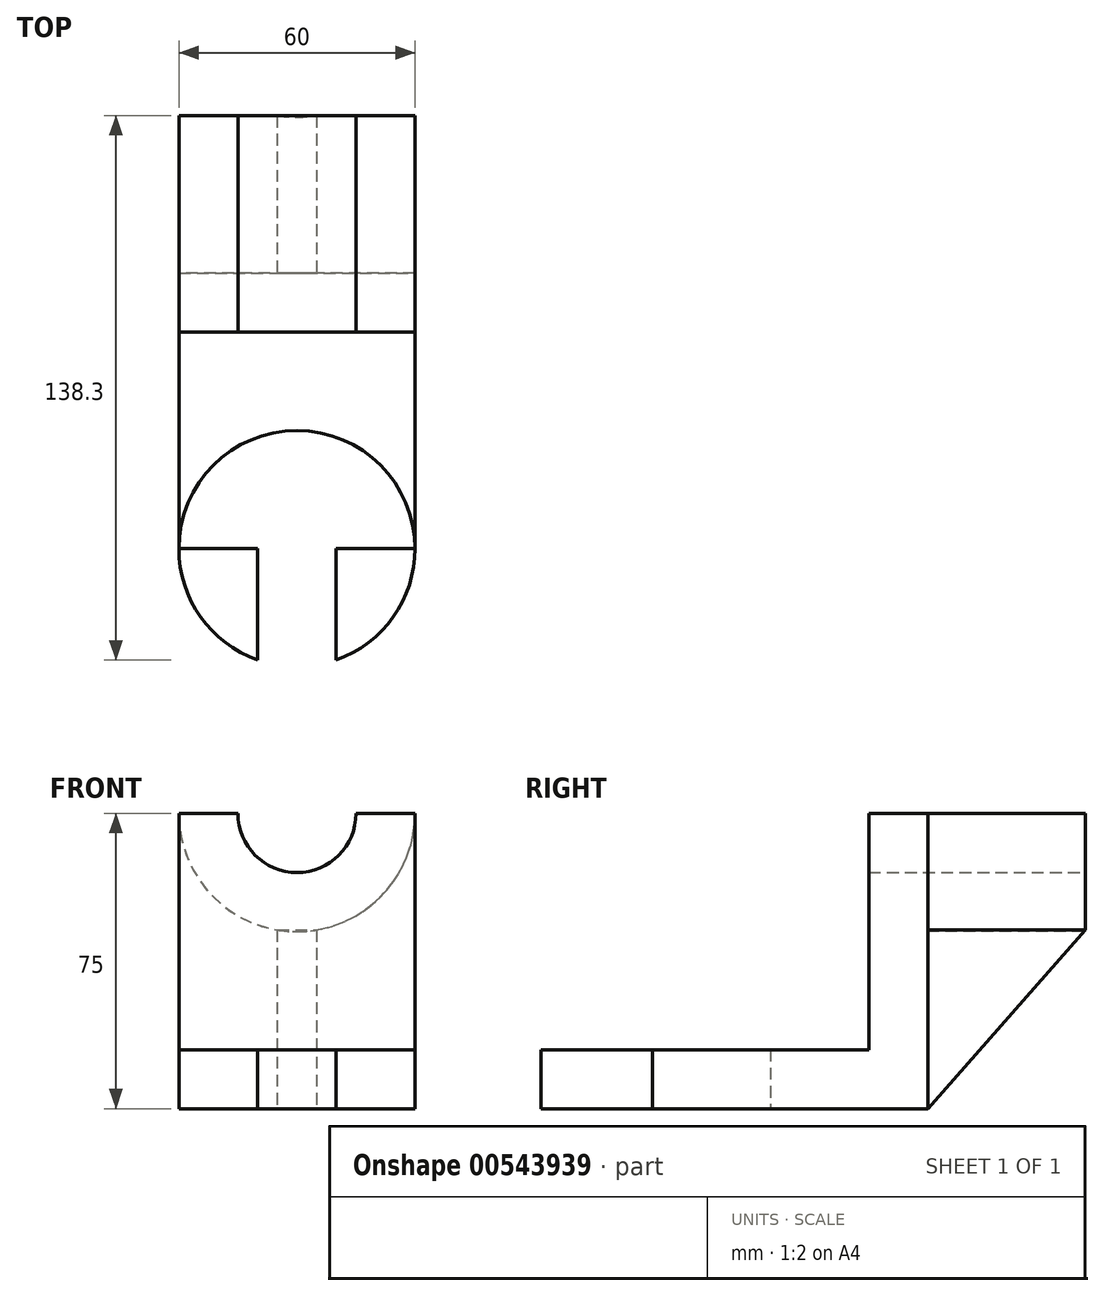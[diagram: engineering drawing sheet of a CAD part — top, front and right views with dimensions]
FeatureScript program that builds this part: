
annotation { "Feature Type Name" : "Feature", "Feature Type Description" : "" }
export const myFeature = defineFeature(function(context is Context, id is Id, definition is map)
    precondition{}
    {
        {
            var Q0;
            Q0=qCreatedBy(makeId("Top.planeOp"),FACE);
            var sketch = newSketch(context, id + "F0", { "sketchPlane" : qUnion([Q0])});
            skLineSegment(sketch, "E0.bottom", {"start": v(-39.95, 26.19) * mm, "end": v(20.05, 26.19) * mm});
            skLineSegment(sketch, "E0.top", {"start": v(-39.95, -43.81) * mm, "end": v(20.05, -43.81) * mm});
            skLineSegment(sketch, "E0.left", {"start": v(-39.95, 26.19) * mm, "end": v(-39.95, -43.81) * mm});
            skLineSegment(sketch, "E0.right", {"start": v(20.05, 26.19) * mm, "end": v(20.05, -43.81) * mm});
            skCircle(sketch, "E1", {"center": v(-9.95, -43.81) * mm, "radius": 30 * mm});
            skLineSegment(sketch, "E2", {"start": v(-9.95, -43.81) * mm, "end": v(-19.95, -43.81) * mm});
            skLineSegment(sketch, "E3", {"start": v(-19.95, -43.81) * mm, "end": v(0.05, -43.81) * mm});
            skLineSegment(sketch, "E4", {"start": v(0.05, -43.81) * mm, "end": v(0, -72.11) * mm});
            skLineSegment(sketch, "E5", {"start": v(-19.95, -43.81) * mm, "end": v(-19.95, -72.1) * mm});
            skLineSegment(sketch, "E6", {"start": v(-39.95, 26.19) * mm, "end": v(-39.95, 11.19) * mm});
            skLineSegment(sketch, "E7", {"start": v(-39.95, 11.19) * mm, "end": v(20.05, 11.19) * mm});
            skSolve(sketch);
        }
        {
            var Q0;
            {var subQ0=sQuery(id+"F0.wireOp",EDGE,"E0.bottom");Q0=makeQuery(id+"F0.imprint","IMPRINT",FACE,{"disambiguationData":[TD([[makeQuery(id+"F0.imprint","IMPRINT",EDGE,{"derivedFrom":subQ0}),-1.0]])]});}
            extrude(context, id + "F1", {"entities" : qUnion([Q0]), "depth" : 75 * mm, "offsetDistance" : 25 * mm});
        }
        {
            var Q0;
            {var subQ0=sQuery(id+"F0.wireOp",EDGE,"E0.left");Q0=makeQuery(id+"F0.imprint","IMPRINT",FACE,{"disambiguationData":[TD([[makeQuery(id+"F0.imprint","IMPRINT",EDGE,{"derivedFrom":subQ0}),1.0]])]});}
            var Q1;
            {var subQ0=sQuery(id+"F0.wireOp",EDGE,"E3");var subQ3=makeQuery(id+"F0.imprint","IMPRINT",VERTEX,{"derivedFrom":subQ0});Q1=makeQuery(id+"F0.imprint","IMPRINT",FACE,{"disambiguationData":[TD([[makeQuery(id+"F0.imprint","IMPRINT",EDGE,{"disambiguationData":[TD([[subQ3,1.0]])],"derivedFrom":subQ0}),1.0]])]});}
            var Q2;
            {var subQ3=sQuery(id+"F0.wireOp",EDGE,"E4");Q2=makeQuery(id+"F0.imprint","IMPRINT",FACE,{"disambiguationData":[TD([[makeQuery(id+"F0.imprint","IMPRINT",EDGE,{"derivedFrom":subQ3}),1.0]])]});}
            var Q3;
            {var subQ0=sQuery(id+"F0.wireOp",EDGE,"E4");Q3=makeQuery(id+"F0.imprint","IMPRINT",FACE,{"disambiguationData":[TD([[makeQuery(id+"F0.imprint","IMPRINT",EDGE,{"derivedFrom":subQ0}),-1.0]])]});}
            var Q4;
            {var subQ3=sQuery(id+"F0.wireOp",EDGE,"E5");Q4=makeQuery(id+"F0.imprint","IMPRINT",FACE,{"disambiguationData":[TD([[makeQuery(id+"F0.imprint","IMPRINT",EDGE,{"derivedFrom":subQ3}),-1.0]])]});}
            extrude(context, id + "F2", {"entities" : qUnion([Q0, Q1, Q2, Q3, Q4]), "operationType" : NewBodyOperationType.ADD, "depth" : 15 * mm, "offsetDistance" : 25 * mm});
        }
        {
            var Q0;
            Q0=makeQuery(id+"F2.opExtrude","CAP_FACE",FACE,{"disambiguationData":[OSD([sQuery(id+"F0.wireOp",EDGE,"E0.left"),sQuery(id+"F0.wireOp",EDGE,"E0.right"),sQuery(id+"F0.wireOp",EDGE,"E1"),sQuery(id+"F0.wireOp",EDGE,"E7")])],"isStart":false});
            var sketch = newSketch(context, id + "F3", { "sketchPlane" : qUnion([Q0])});
            skLineSegment(sketch, "E8.0.0", {"start": v(-39.95, 11.19) * mm, "end": v(-39.95, -43.81) * mm});
            skArc(sketch, "E8.0.1", {"start": v(-39.95, -43.81) * mm, "mid": v(-9.95, -73.81) * mm, "end": v(20.05, -43.81) * mm});
            skLineSegment(sketch, "E8.0.2", {"start": v(20.05, -43.81) * mm, "end": v(20.05, 11.19) * mm});
            skLineSegment(sketch, "E8.0.3", {"start": v(20.05, 11.19) * mm, "end": v(-39.95, 11.19) * mm});
            skCircle(sketch, "E9.0", {"center": v(-9.95, -43.81) * mm, "radius": 30 * mm});
            skPoint(sketch, "E10.0", {"position": v(-19.95, -43.81) * mm});
            skLineSegment(sketch, "E11.0", {"start": v(-39.95, -43.81) * mm, "end": v(20.05, -43.81) * mm});
            skPoint(sketch, "E12.0", {"position": v(0.02, -57.96) * mm});
            skLineSegment(sketch, "E13.0", {"start": v(0.05, -43.81) * mm, "end": v(0, -72.11) * mm});
            skLineSegment(sketch, "E14.0", {"start": v(-19.95, -43.81) * mm, "end": v(-19.95, -72.1) * mm});
            skSolve(sketch);
        }
        {
            var Q0;
            {var subQ0=sQuery(id+"F3.wireOp",EDGE,"E13.0");Q0=makeQuery(id+"F3.imprint","IMPRINT",FACE,{"disambiguationData":[TD([[makeQuery(id+"F3.imprint","IMPRINT",EDGE,{"derivedFrom":subQ0}),-1.0]])]});}
            extrude(context, id + "F4", {"entities" : qUnion([Q0]), "operationType" : NewBodyOperationType.REMOVE, "oppositeDirection" : true, "depth" : 41.2 * mm, "offsetDistance" : 25 * mm});
        }
        {
            var Q0;
            Q0=makeQuery(id+"F1.opExtrude","SWEPT_FACE",FACE,{"disambiguationData":[OSD([sQuery(id+"F0.wireOp",EDGE,"E0.bottom")])]});
            var sketch = newSketch(context, id + "F5", { "sketchPlane" : qUnion([Q0])});
            skArc(sketch, "E15", {"start": v(-5.05, 75) * mm, "mid": v(9.95, 60) * mm, "end": v(24.95, 75) * mm});
            skLineSegment(sketch, "E16", {"start": v(-20.05, 75) * mm, "end": v(39.95, 75) * mm});
            skArc(sketch, "E17", {"start": v(-20.05, 75) * mm, "mid": v(9.95, 45) * mm, "end": v(39.95, 75) * mm});
            skSolve(sketch);
        }
        {
            var Q0;
            Q0 = qSketchRegion(id + "F5", true);
            extrude(context, id + "F6", {"entities" : qUnion([Q0]), "operationType" : NewBodyOperationType.ADD, "depth" : 40 * mm, "offsetDistance" : 25 * mm});
        }
        {
            var Q0;
            Q0=makeQuery(id+"F6.opExtrude","CAP_FACE",FACE,{"disambiguationData":[OSD([sQuery(id+"F5.wireOp",EDGE,"E16"),sQuery(id+"F5.wireOp",EDGE,"E17")])],"isStart":false});
            var sketch = newSketch(context, id + "F7", { "sketchPlane" : qUnion([Q0])});
            skCircle(sketch, "E18", {"center": v(9.95, 75) * mm, "radius": 15 * mm});
            skSolve(sketch);
        }
        {
            var Q0;
            Q0 = qSketchRegion(id + "F7", true);
            extrude(context, id + "F8", {"entities" : qUnion([Q0]), "operationType" : NewBodyOperationType.REMOVE, "oppositeDirection" : true, "depth" : 168.2 * mm, "offsetDistance" : 25 * mm});
        }
        {
            var Q0;
            Q0=makeQuery(id+"F1.opExtrude","SWEPT_FACE",FACE,{"disambiguationData":[OSD([sQuery(id+"F0.wireOp",EDGE,"E0.bottom")])]});
            var sketch = newSketch(context, id + "F9", { "sketchPlane" : qUnion([Q0])});
            skLineSegment(sketch, "E19", {"start": v(-20.05, 0) * mm, "end": v(4.95, 0) * mm});
            skLineSegment(sketch, "E20", {"start": v(4.95, 0) * mm, "end": v(14.95, 0) * mm});
            skLineSegment(sketch, "E21", {"start": v(14.95, 0) * mm, "end": v(14.95, 45.42) * mm});
            skLineSegment(sketch, "E22", {"start": v(14.95, 45.42) * mm, "end": v(4.95, 0) * mm});
            skLineSegment(sketch, "E23", {"start": v(4.95, 0) * mm, "end": v(4.95, 45.42) * mm});
            skSolve(sketch);
        }
        {
            var Q0;
            Q0=makeQuery(id+"F9.imprint","IMPRINT",FACE,{"disambiguationData":[TD([[makeQuery(id+"F9.imprint","IMPRINT",EDGE,{"derivedFrom":sQuery(id+"F9.wireOp",EDGE,"E20")}),-1.0]])]});
            var Q1;
            {var subQ0=sQuery(id+"F9.wireOp",EDGE,"E22");Q1=makeQuery(id+"F9.imprint","IMPRINT",FACE,{"disambiguationData":[TD([[makeQuery(id+"F9.imprint","IMPRINT",EDGE,{"derivedFrom":subQ0}),-1.0]])]});}
            extrude(context, id + "F10", {"entities" : qUnion([Q0, Q1]), "depth" : 40 * mm, "offsetDistance" : 25 * mm});
        }
        {
            var Q0;
            Q0=makeQuery(id+"F10.opExtrude","SWEPT_FACE",FACE,{"disambiguationData":[OSD([sQuery(id+"F9.wireOp",EDGE,"E23")])]});
            var sketch = newSketch(context, id + "F11", { "sketchPlane" : qUnion([Q0])});
            skLineSegment(sketch, "E24", {"start": v(66.19, 45.42) * mm, "end": v(26.19, 0) * mm});
            skSolve(sketch);
        }
        {
            var Q0;
            Q0 = qSketchRegion(id + "F11", true);
            var Q1;
            Q1=makeQuery(id+"F11.imprint","IMPRINT",FACE,{"disambiguationData":[TD([[makeQuery(id+"F11.imprint","IMPRINT",EDGE,{"derivedFrom":sQuery(id+"F11.wireOp",EDGE,"E24")}),1.0]])]});
            extrude(context, id + "F12", {"entities" : qUnion([Q0, Q1]), "operationType" : NewBodyOperationType.REMOVE, "oppositeDirection" : true, "depth" : 25 * mm, "offsetDistance" : 25 * mm});
        }
    });
